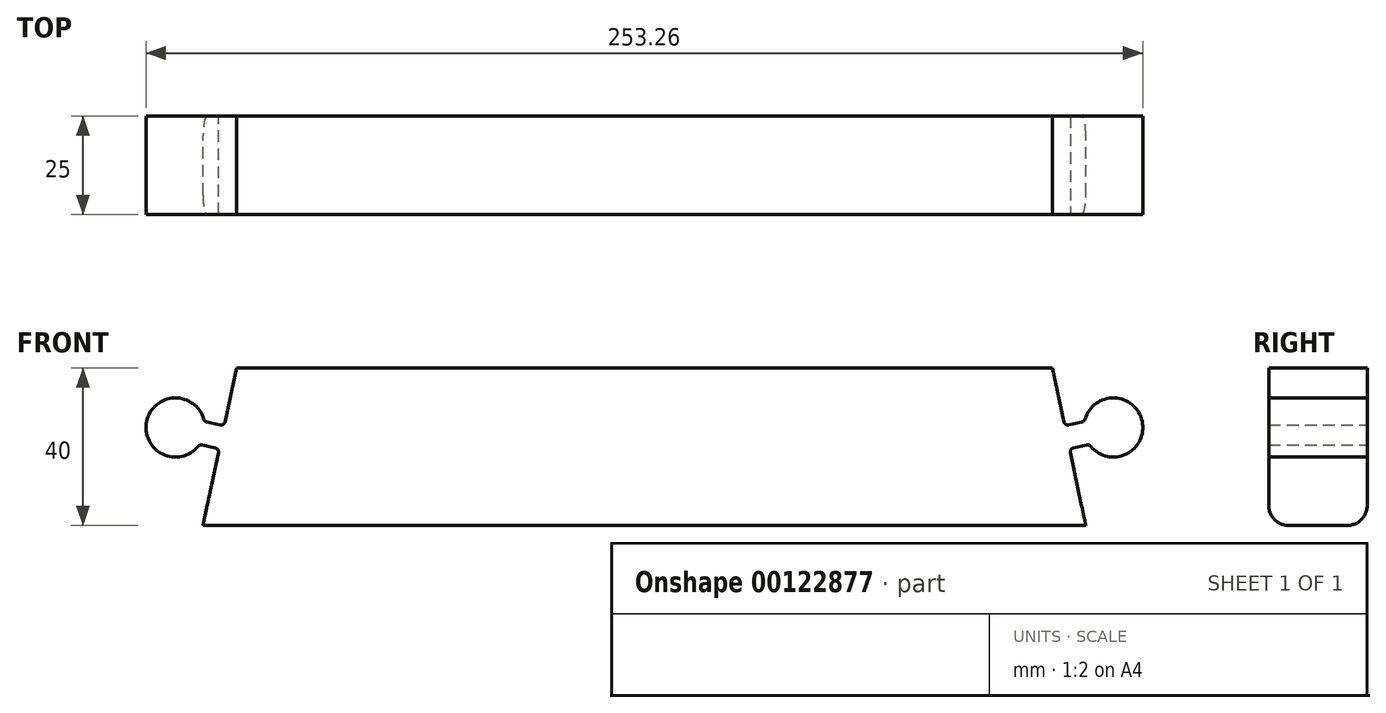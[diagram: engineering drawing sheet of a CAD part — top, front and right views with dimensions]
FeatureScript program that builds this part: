
annotation { "Feature Type Name" : "Feature", "Feature Type Description" : "" }
export const myFeature = defineFeature(function(context is Context, id is Id, definition is map)
    precondition{}
    {
        {
            var Q0;
            Q0=qCreatedBy(makeId("Front.planeOp"),FACE);
            var sketch = newSketch(context, id + "F0", { "sketchPlane" : qUnion([Q0])});
            skLineSegment(sketch, "E0", {"start": v(-77.61, 40) * mm, "end": v(129.69, 40) * mm});
            skLineSegment(sketch, "E1", {"start": v(129.69, 40) * mm, "end": v(132.8, 25.33) * mm});
            skLineSegment(sketch, "E2", {"start": v(138.2, 0) * mm, "end": v(-86.11, 0) * mm});
            skLineSegment(sketch, "E3", {"start": v(-86.11, 0) * mm, "end": v(-81.98, 19.46) * mm});
            skLineSegment(sketch, "E4", {"start": v(132.8, 25.33) * mm, "end": v(137.82, 26.4) * mm});
            skLineSegment(sketch, "E5", {"start": v(139.07, 20.52) * mm, "end": v(134.05, 19.46) * mm});
            skArc(sketch, "E6", {"start": v(139.07, 20.52) * mm, "mid": v(152.5, 26.45) * mm, "end": v(137.82, 26.4) * mm});
            skPoint(sketch, "E6.centerSnap0", {"position": v(145.17, 24.89) * mm});
            skLineSegment(sketch, "E7.trimOffspring", {"start": v(134.05, 19.46) * mm, "end": v(138.2, 0) * mm});
            skPoint(sketch, "E8.orphan", {"position": v(145.17, 27.96) * mm});
            skPoint(sketch, "E9.orphan", {"position": v(145.17, 21.82) * mm});
            skLineSegment(sketch, "E10", {"start": v(-80.73, 25.33) * mm, "end": v(-85.74, 26.4) * mm});
            skLineSegment(sketch, "E11", {"start": v(-87, 20.52) * mm, "end": v(-81.98, 19.46) * mm});
            skArc(sketch, "E12", {"start": v(-85.74, 26.4) * mm, "mid": v(-100.43, 26.45) * mm, "end": v(-87, 20.52) * mm});
            skLineSegment(sketch, "E13.trimOffspring", {"start": v(-80.73, 25.33) * mm, "end": v(-77.61, 40) * mm});
            skPoint(sketch, "E14.orphan", {"position": v(-93.72, 21.95) * mm});
            skPoint(sketch, "E15.start.orphan", {"position": v(-92.47, 27.82) * mm});
            skSolve(sketch);
        }
        {
            var Q0;
            Q0=makeQuery(id+"F0.imprint","IMPRINT",FACE,{"disambiguationData":[TD([[makeQuery(id+"F0.imprint","IMPRINT",EDGE,{"derivedFrom":sQuery(id+"F0.wireOp",EDGE,"E0")}),-1.0]])]});
            extrude(context, id + "F1", {"entities" : qUnion([Q0]), "depth" : 25 * mm});
        }
        {
            var Q0;
            Q0=makeQuery(id+"F1.opExtrude","SWEPT_EDGE",EDGE,{"disambiguationData":[OSD([sQuery(id+"F0.wireOp",EDGE,"E5"),sQuery(id+"F0.wireOp",EDGE,"E7.trimOffspring")])]});
            var Q1;
            Q1=makeQuery(id+"F1.opExtrude","SWEPT_EDGE",EDGE,{"disambiguationData":[OSD([sQuery(id+"F0.wireOp",EDGE,"E5"),sQuery(id+"F0.wireOp",EDGE,"E6")])]});
            var Q2;
            Q2=makeQuery(id+"F1.opExtrude","SWEPT_EDGE",EDGE,{"disambiguationData":[OSD([sQuery(id+"F0.wireOp",EDGE,"E1"),sQuery(id+"F0.wireOp",EDGE,"E4")])]});
            var Q3;
            Q3=makeQuery(id+"F1.opExtrude","SWEPT_EDGE",EDGE,{"disambiguationData":[OSD([sQuery(id+"F0.wireOp",EDGE,"E4"),sQuery(id+"F0.wireOp",EDGE,"E6")])]});
            var Q4;
            Q4=makeQuery(id+"F1.opExtrude","SWEPT_EDGE",EDGE,{"disambiguationData":[OSD([sQuery(id+"F0.wireOp",EDGE,"E10"),sQuery(id+"F0.wireOp",EDGE,"E12")])]});
            var Q5;
            Q5=makeQuery(id+"F1.opExtrude","SWEPT_EDGE",EDGE,{"disambiguationData":[OSD([sQuery(id+"F0.wireOp",EDGE,"E10"),sQuery(id+"F0.wireOp",EDGE,"E13.trimOffspring")])]});
            var Q6;
            Q6=makeQuery(id+"F1.opExtrude","SWEPT_EDGE",EDGE,{"disambiguationData":[OSD([sQuery(id+"F0.wireOp",EDGE,"E3"),sQuery(id+"F0.wireOp",EDGE,"E11")])]});
            var Q7;
            Q7=makeQuery(id+"F1.opExtrude","SWEPT_EDGE",EDGE,{"disambiguationData":[OSD([sQuery(id+"F0.wireOp",EDGE,"E11"),sQuery(id+"F0.wireOp",EDGE,"E12")])]});
            fillet(context, id + "F2", {"entities" : qUnion([Q0, Q1, Q2, Q3, Q4, Q5, Q6, Q7]), "radius" : 1 * mm, "tangentPropagation" : true, "allowEdgeOverflow" : false});
        }
        {
            var Q0;
            Q0=makeQuery(id+"F1.opExtrude","CAP_EDGE",EDGE,{"disambiguationData":[OSD([sQuery(id+"F0.wireOp",EDGE,"E2")])],"isStart":false});
            var Q1;
            Q1=makeQuery(id+"F1.opExtrude","CAP_EDGE",EDGE,{"disambiguationData":[OSD([sQuery(id+"F0.wireOp",EDGE,"E2")])],"isStart":true});
            fillet(context, id + "F3", {"entities" : qUnion([Q0, Q1]), "radius" : 5 * mm, "tangentPropagation" : true, "allowEdgeOverflow" : false});
        }
    });
